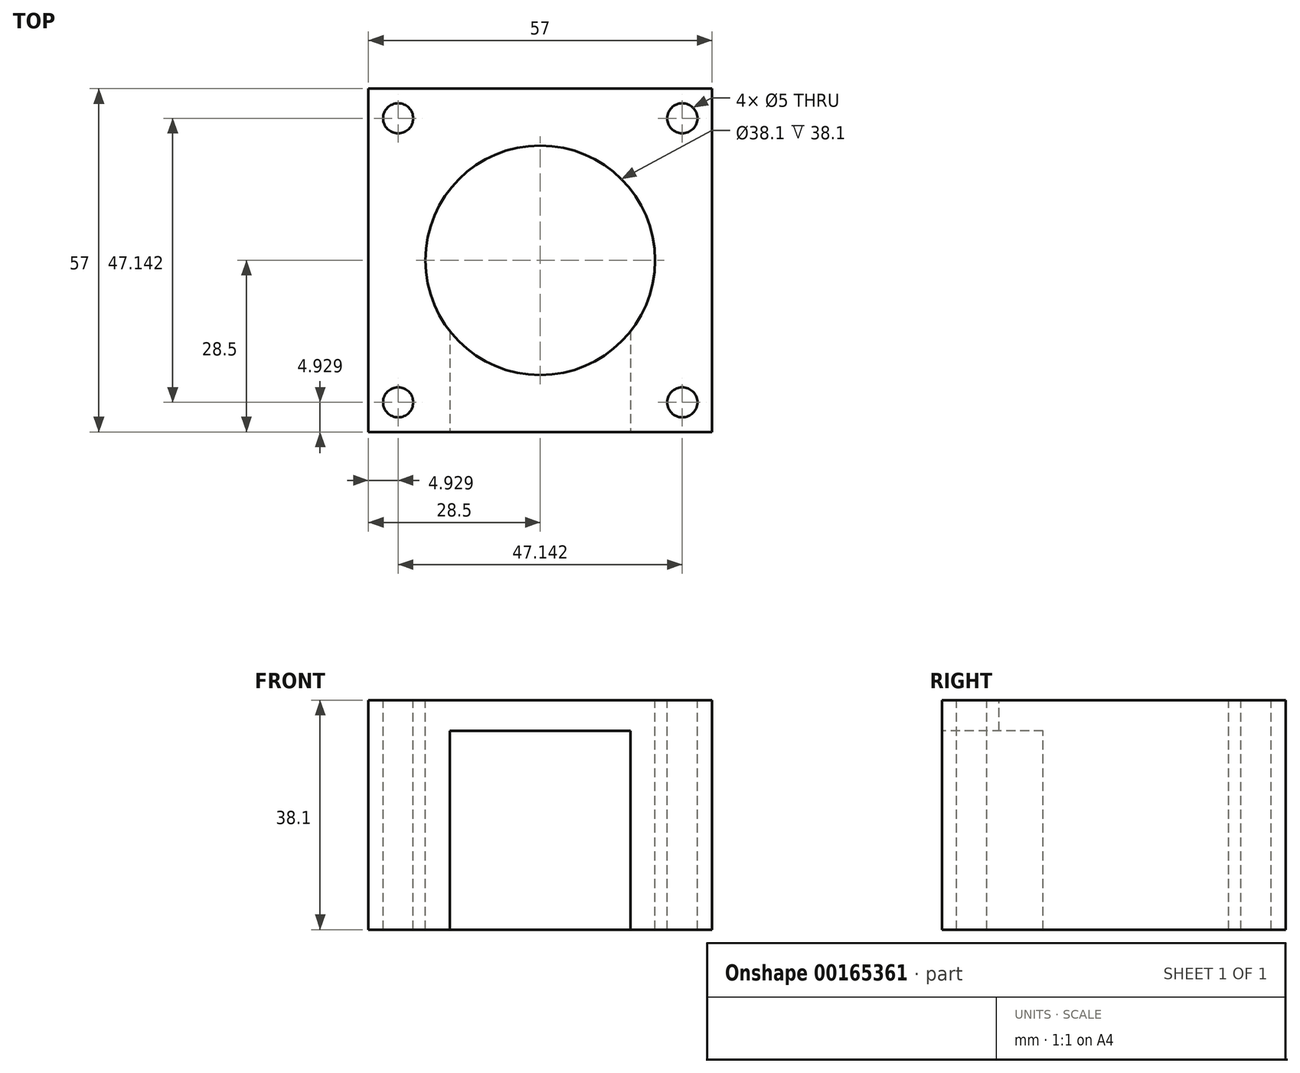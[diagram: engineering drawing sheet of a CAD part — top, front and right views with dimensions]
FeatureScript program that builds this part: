
annotation { "Feature Type Name" : "Feature", "Feature Type Description" : "" }
export const myFeature = defineFeature(function(context is Context, id is Id, definition is map)
    precondition{}
    {
        {
            var Q0;
            Q0=qCreatedBy(makeId("Top.planeOp"),FACE);
            var sketch = newSketch(context, id + "F0", { "sketchPlane" : qUnion([Q0])});
            skLineSegment(sketch, "E0.rect.bottom", {"start": v(28.5, -28.5) * mm, "end": v(-28.5, -28.5) * mm});
            skLineSegment(sketch, "E0.rect.top", {"start": v(28.5, 28.5) * mm, "end": v(-28.5, 28.5) * mm});
            skLineSegment(sketch, "E0.rect.left", {"start": v(28.5, -28.5) * mm, "end": v(28.5, 28.5) * mm});
            skLineSegment(sketch, "E0.rect.right", {"start": v(-28.5, -28.5) * mm, "end": v(-28.5, 28.5) * mm});
            skPoint(sketch, "E0.rect.middle", {"position": v(0, 0) * mm});
            skSolve(sketch);
        }
        {
            var Q0;
            Q0=qSketchRegion(id+"F0",true);
            extrude(context, id + "F1", {"entities" : qUnion([Q0]), "depth" : 38.1 * mm});
        }
        {
            var Q0;
            Q0=makeQuery(id+"F1.opExtrude","SWEPT_FACE",FACE,{"disambiguationData":[OSD([sQuery(id+"F0.wireOp",EDGE,"E0.rect.bottom")])]});
            var sketch = newSketch(context, id + "F2", { "sketchPlane" : qUnion([Q0])});
            skLineSegment(sketch, "E1", {"start": v(0, 0) * mm, "end": v(15, 0) * mm});
            skLineSegment(sketch, "E2", {"start": v(15, 0) * mm, "end": v(0, 0) * mm});
            skLineSegment(sketch, "E3", {"start": v(-15, 0) * mm, "end": v(0, 0) * mm});
            skLineSegment(sketch, "E4", {"start": v(-15, 0) * mm, "end": v(-15, 33) * mm});
            skLineSegment(sketch, "E5", {"start": v(-15, 33) * mm, "end": v(15, 33) * mm});
            skLineSegment(sketch, "E6", {"start": v(15, 33) * mm, "end": v(15, 0) * mm});
            skSolve(sketch);
        }
        {
            var Q0;
            Q0=qSketchRegion(id+"F2",true);
            extrude(context, id + "F3", {"entities" : qUnion([Q0]), "operationType" : NewBodyOperationType.REMOVE, "oppositeDirection" : true, "depth" : 28.5 * mm});
        }
        {
            var Q0;
            Q0=makeQuery(id+"F1.opExtrude","CAP_FACE",FACE,{"disambiguationData":[OSD([sQuery(id+"F0.wireOp",EDGE,"E0.rect.bottom"),sQuery(id+"F0.wireOp",EDGE,"E0.rect.top"),sQuery(id+"F0.wireOp",EDGE,"E0.rect.left"),sQuery(id+"F0.wireOp",EDGE,"E0.rect.right")])],"isStart":false});
            var sketch = newSketch(context, id + "F4", { "sketchPlane" : qUnion([Q0])});
            skCircle(sketch, "E7", {"center": v(0, 0) * mm, "radius": 19.05 * mm});
            skSolve(sketch);
        }
        {
            var Q0;
            Q0=qSketchRegion(id+"F4",true);
            extrude(context, id + "F5", {"entities" : qUnion([Q0]), "operationType" : NewBodyOperationType.REMOVE, "endBound" : BoundingType.THROUGH_ALL, "oppositeDirection" : true, "depth" : 25.4 * mm});
        }
        {
            var Q0;
            Q0=makeQuery(id+"F1.opExtrude","CAP_FACE",FACE,{"disambiguationData":[OSD([sQuery(id+"F0.wireOp",EDGE,"E0.rect.bottom"),sQuery(id+"F0.wireOp",EDGE,"E0.rect.top"),sQuery(id+"F0.wireOp",EDGE,"E0.rect.left"),sQuery(id+"F0.wireOp",EDGE,"E0.rect.right")])],"isStart":false});
            var sketch = newSketch(context, id + "F6", { "sketchPlane" : qUnion([Q0])});
            skPoint(sketch, "E8.rect.middle", {"position": v(0, 0) * mm});
            skCircle(sketch, "E9", {"center": v(-23.57, 23.57) * mm, "radius": 2.5 * mm});
            skCircle(sketch, "E10", {"center": v(23.57, 23.57) * mm, "radius": 2.5 * mm});
            skCircle(sketch, "E11", {"center": v(23.57, -23.57) * mm, "radius": 2.5 * mm});
            skCircle(sketch, "E12", {"center": v(-23.57, -23.57) * mm, "radius": 2.5 * mm});
            skSolve(sketch);
        }
        {
            var Q0;
            Q0=qSketchRegion(id+"F6",true);
            extrude(context, id + "F7", {"entities" : qUnion([Q0]), "operationType" : NewBodyOperationType.REMOVE, "endBound" : BoundingType.THROUGH_ALL, "oppositeDirection" : true, "depth" : 25.4 * mm});
        }
    });
